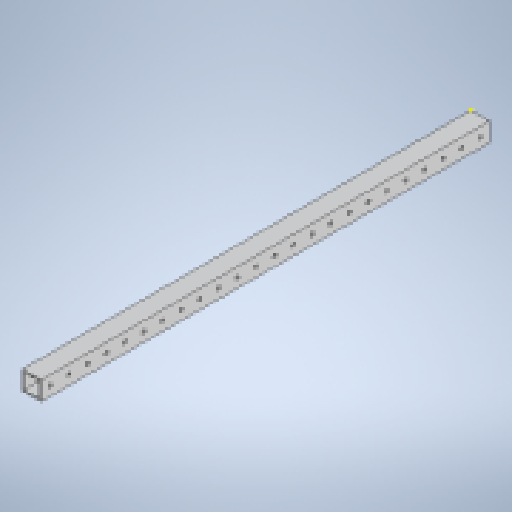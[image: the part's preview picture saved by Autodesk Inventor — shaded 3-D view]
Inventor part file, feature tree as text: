
AUTODESK INVENTOR PART (.ipt)
format: ipt  version: 2024 (Build 280153000, 153)  size: 217,600 bytes
history: native  units: in
note: dims shown in document units (in); Inventor stores cm internally (conversion verified against a paired STEP export)
features: extrude x3, sketch x2, pattern_linear x1
ambient origin geometry x8: Origin, YZ Plane, XZ Plane, XY Plane, X Axis, Y Axis, Z Axis, Center Point
bodies: Solid1 (feature_tree)
feature tree (6):
  extrude  "Extrusion1"  Depth=1.0in
  extrude  "Extrusion2"  Depth=25.0in TaperAngle=0.0deg
  pattern_linear  "Rectangular Pattern1"  Spacing1=0.201in  [1 undecoded]
  sketch  "Sketch4"  dims[d0=1.0in d1=1.0in]
  extrude  "Extrusion3"  Depth=25.0in
  sketch  "Sketch5"  dims[d2=0.09in d3=25.0in d4=0.0in d5=0.201in d6=0.5in d7=0.5in d8=24.0in d9=0.0in d10=9.8425in d12=1.0in d13=0.5in d14=0.5in d15=0.375in d16=0.375in d17=4.07in d18=0.5in d19=0.375in d20=0.375in d21=4.07in d22=0.5in d23=0.5in d24=0.5in d25=25.0in d26=0.0in]
note: 1 required parameter value undecoded (feature->parameter linkage not recoverable at this tier; creation-order binding heuristic only, values carry confidence <= 0.55)
